# Revit family: MT-ThermAFrame CP FRAMING CA DBL GLZ
name_source: partatom
category: Windows
revit_build: Autodesk Revit 2017 (Build: 20160225_1515(x64)
units: mm (PartAtom-declared; Revit-internal decimal feet)

## family parameters
Always vertical = Yes
Cut with Voids When Loaded = No
Host = Wall
OmniClass Number = 23.30.20.00
OmniClass Title = Windows
Room Calculation Point = No
Shared = No

## types (2) — shared parameters
AIR POCKET = 13 mm
ANZRC COMPLIANT = YES
BOT PANEL POSITION = 50 mm
DOUBLE GLAZED THICKNESS = 25 mm  [stored 0.082021 ft]
Default Sill Height = 900 mm  [stored 2.95276 ft]
FRAME MATERIAL = <By Category>
FRAME THICKNESS = 102 mm
GLAZED MATERIAL = Glass
Height = 1800 mm
MAX HEIGHT = 2000 mm  [stored 6.56168 ft]
MAX PANEL HEIGHT = 2000 mm  [stored 6.56168 ft]
MAX PANEL WIDTH = 1500 mm  [stored 4.92126 ft]
MAX WIDTH = 1500 mm  [stored 4.92126 ft]
Manufacturer = ALSPEC
Model = HAWKESBURY TOP HUNG COMMERCIAL SLIDING DOOR
OFFSET = 10 mm  [stored 0.0328084 ft]
OVERALL FRAME HEIGHT = 1800 mm
OVERALL FRAME WIDTH = 1500 mm  [stored 4.92126 ft]
PANEL HEIGHT = 1700 mm  [stored 5.57743 ft]
PANEL WIDTH = 1400 mm  [stored 4.59318 ft]
Rough Height = 1900 mm  [stored 6.2336 ft]
Rough Width = 1600 mm  [stored 5.24934 ft]
SINGLE GLAZED THICKNESS = 5 mm  [stored 0.0164042 ft]
TOLERANCE = 50 mm
URL = WWW.ALSPEC.COM.AU
VERSION = 2.1
WARNING = No
Wall Closure = By host
Width = 1500 mm  [stored 4.92126 ft]
YEAR = 2019

## per-type parameters (varying)
| type | 150mm CP FRAMING |
| ASW100 MITRED ADAPTOR | Yes |
| 101.6mm CP FRAMING | No |

type visibility flags (boolean, named after types; folded from table):
- ASW100 MITRED ADAPTOR: Yes: (none)
- 101.6mm CP FRAMING: Yes: 101.6mm CP FRAMING

note: [stored X ft] marks values corroborated as IEEE doubles in the binary element streams (Revit-internal decimal feet)

## geometry (parser evidence)
native form markers: Sweep x12
no freeform markers — native parametric forms only
